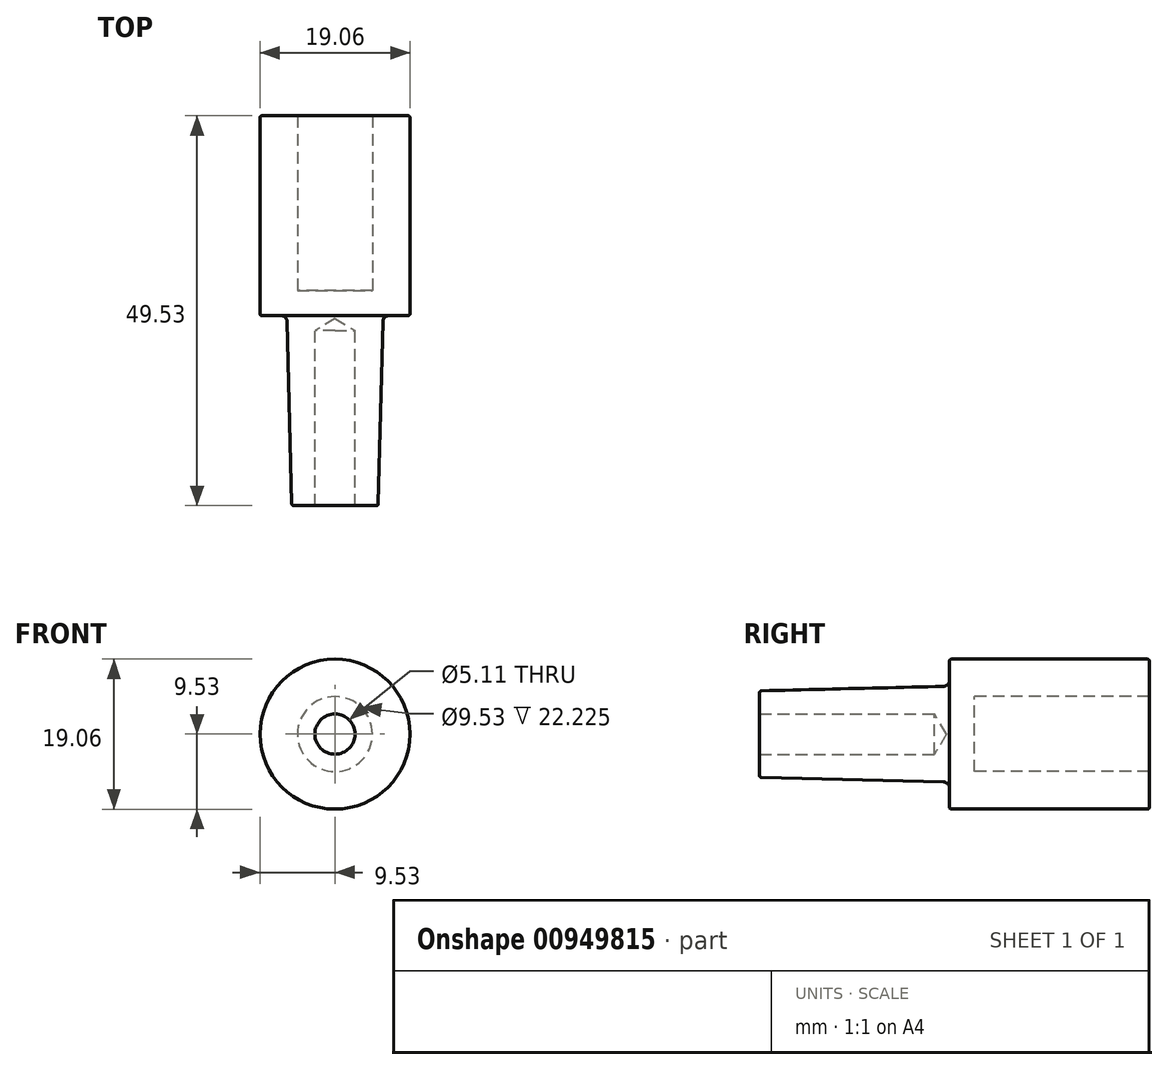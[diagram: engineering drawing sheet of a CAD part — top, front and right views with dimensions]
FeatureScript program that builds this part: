
annotation { "Feature Type Name" : "Feature", "Feature Type Description" : "" }
export const myFeature = defineFeature(function(context is Context, id is Id, definition is map)
    precondition{}
    {
        {
            var Q0;
            Q0=qCreatedBy(makeId("Right.planeOp"),FACE);
            var sketch = newSketch(context, id + "F0", { "sketchPlane" : qUnion([Q0])});
            skLineSegment(sketch, "E0", {"start": v(25.4, 0) * mm, "end": v(25.4, 9.53) * mm});
            skLineSegment(sketch, "E1", {"start": v(25.4, 9.53) * mm, "end": v(0, 9.53) * mm});
            skLineSegment(sketch, "E2", {"start": v(0, 9.53) * mm, "end": v(0, 6.1) * mm});
            skLineSegment(sketch, "E3", {"start": v(0, 6.1) * mm, "end": v(-24.13, 5.5) * mm});
            skLineSegment(sketch, "E4", {"start": v(-24.13, 5.5) * mm, "end": v(-24.13, 0) * mm});
            skLineSegment(sketch, "E5", {"start": v(-24.13, 0) * mm, "end": v(25.4, 0) * mm});
            skLineSegment(sketch, "E6", {"start": v(-59.9, 0) * mm, "end": v(67.6, 0) * mm, "construction": true});
            skSolve(sketch);
        }
        {
            var Q0;
            Q0=qSketchRegion(id+"F0",true);
            var Q1;
            Q1=sQuery(id+"F0.wireOp",EDGE,"E5");
            revolve(context, id + "F1", {"surfaceOperationType" : NewSurfaceOperationType.NEW, "entities" : qUnion([Q0]), "axis" : qUnion([Q1]), "revolveType" : RevolveType.FULL});
        }
        {
            var Q0;
            Q0=makeQuery(id+"F1.opRevolve","SWEPT_FACE",FACE,{"disambiguationData":[OSD([sQuery(id+"F0.wireOp",EDGE,"E4")])]});
            var sketch = newSketch(context, id + "F2", { "sketchPlane" : qUnion([Q0])});
            skPoint(sketch, "E7", {"position": v(0, 0) * mm});
            skSolve(sketch);
        }
        {
            var Q0;
            Q0=sQuery(id+"F2.wireOp",VERTEX,"E7");
            var Q1;
            Q1=makeQuery(id+"F1.opRevolve","SWEPT_BODY",BODY,{"disambiguationData":[OSD([sQuery(id+"F0.wireOp",EDGE,"E0"),sQuery(id+"F0.wireOp",EDGE,"E1"),sQuery(id+"F0.wireOp",EDGE,"E2"),sQuery(id+"F0.wireOp",EDGE,"E3"),sQuery(id+"F0.wireOp",EDGE,"E4"),sQuery(id+"F0.wireOp",EDGE,"E5")])]});
            hole(context, id + "F3", {"style" : HoleStyle.SIMPLE, "endStyle" : HoleEndStyle.BLIND, "standardTappedOrClearance" : lookupTablePath({ "standard" : "ANSI", "engagement" : "75%", "pitch" : "20 tpi", "size" : "1/4", "type" : "Tapped" }), "standardBlindInLast" : lookupTablePath({ "standard" : "ANSI", "engagement" : "75%", "pitch" : "20 tpi", "size" : "1/4", "type" : "Tapped" }), "holeDiameter" : 5.1 * mm, "showTappedDepth" : true, "holeDepth" : 22.22 * mm, "isTappedThrough" : true, "tappedDepth" : 18.41 * mm, "tapClearance" : 3, "startFromSketch" : true, "locations" : qUnion([Q0]), "scope" : qUnion([Q1]), "majorDiameter" : 6.35 * mm});
        }
        {
            var Q0;
            Q0=makeQuery(id+"F1.opRevolve","SWEPT_EDGE",EDGE,{"disambiguationData":[OSD([sQuery(id+"F0.wireOp",EDGE,"E2"),sQuery(id+"F0.wireOp",EDGE,"E3")])]});
            fillet(context, id + "F4", {"entities" : qUnion([Q0]), "radius" : 0.76 * mm, "tangentPropagation" : true, "allowEdgeOverflow" : false});
        }
        {
            var Q0;
            Q0=makeQuery(id+"F1.opRevolve","SWEPT_EDGE",EDGE,{"disambiguationData":[OSD([sQuery(id+"F0.wireOp",EDGE,"E1"),sQuery(id+"F0.wireOp",EDGE,"E2")])]});
            var Q1;
            Q1=makeQuery(id+"F1.opRevolve","SWEPT_EDGE",EDGE,{"disambiguationData":[OSD([sQuery(id+"F0.wireOp",EDGE,"E0"),sQuery(id+"F0.wireOp",EDGE,"E1")])]});
            var Q2;
            Q2=makeQuery(id+"F1.opRevolve","SWEPT_EDGE",EDGE,{"disambiguationData":[OSD([sQuery(id+"F0.wireOp",EDGE,"E3"),sQuery(id+"F0.wireOp",EDGE,"E4")])]});
            fillet(context, id + "F5", {"entities" : qUnion([Q0, Q1, Q2]), "radius" : 0.25 * mm, "tangentPropagation" : true, "allowEdgeOverflow" : false});
        }
        {
            var Q0;
            Q0=qCreatedBy(makeId("Right.planeOp"),FACE);
            var sketch = newSketch(context, id + "F6", { "sketchPlane" : qUnion([Q0])});
            skLineSegment(sketch, "E8.bottom", {"start": v(50.22, 0) * mm, "end": v(3.18, 0) * mm});
            skLineSegment(sketch, "E8.top", {"start": v(50.22, 4.76) * mm, "end": v(3.18, 4.76) * mm});
            skLineSegment(sketch, "E8.left", {"start": v(50.22, 0) * mm, "end": v(50.22, 4.76) * mm});
            skLineSegment(sketch, "E8.right", {"start": v(3.18, 0) * mm, "end": v(3.18, 4.76) * mm});
            skSolve(sketch);
        }
        {
            var Q0;
            Q0 = qSketchRegion(id + "F6", true);
            var Q1;
            Q1=sQuery(id+"F6.wireOp",EDGE,"E8.bottom");
            revolve(context, id + "F7", {"operationType" : NewBodyOperationType.REMOVE, "surfaceOperationType" : NewSurfaceOperationType.NEW, "entities" : qUnion([Q0]), "axis" : qUnion([Q1]), "revolveType" : RevolveType.FULL, "oppositeDirection" : true});
        }
    });
